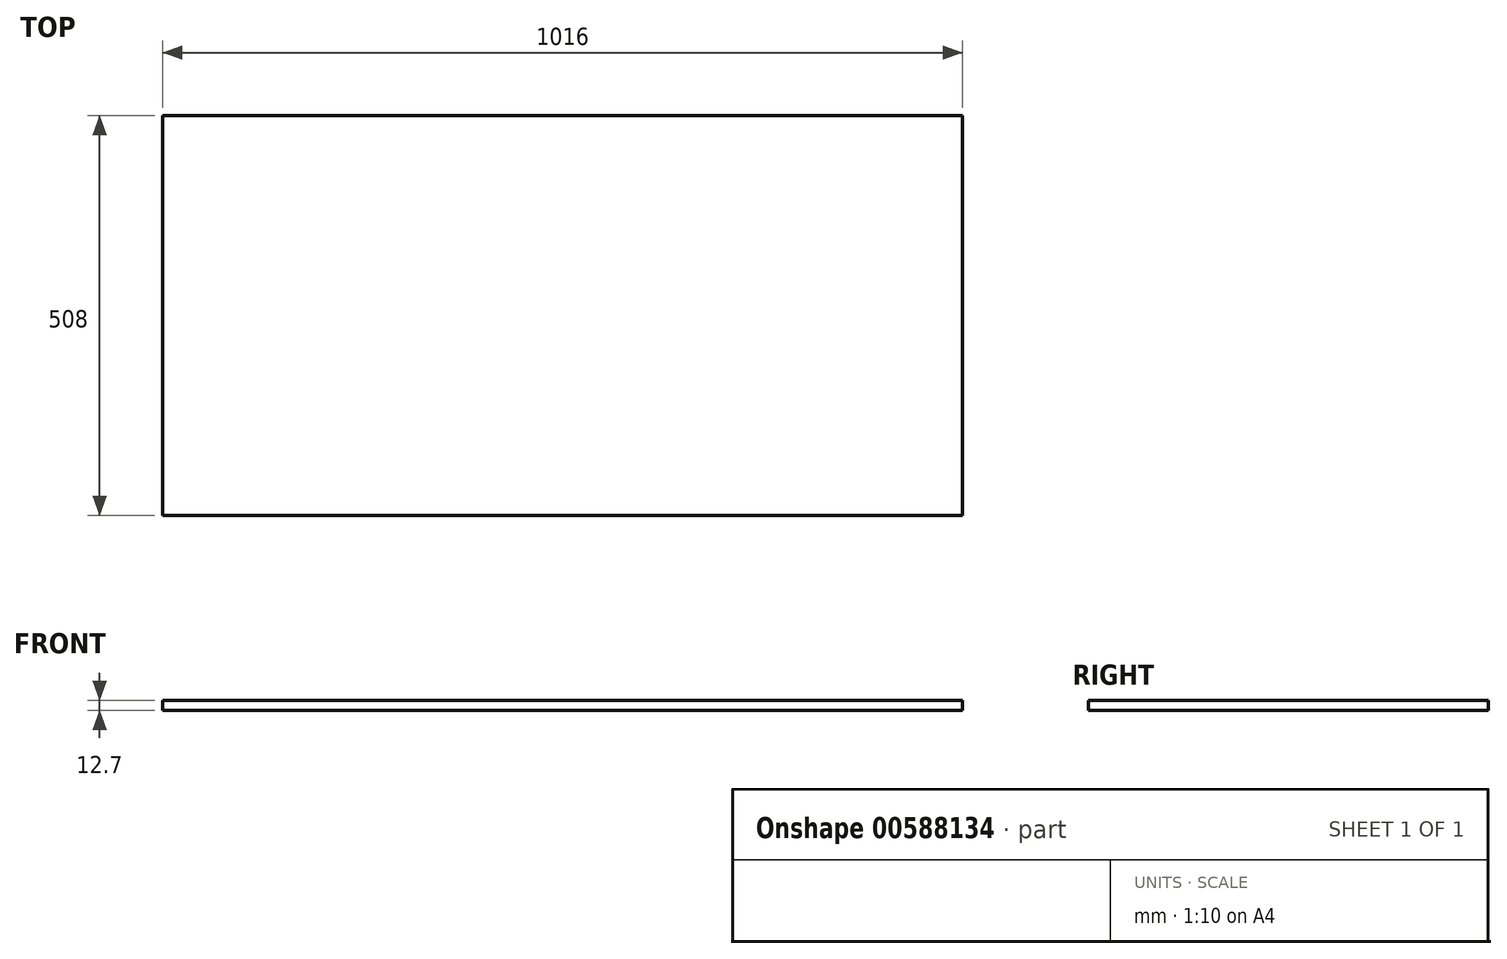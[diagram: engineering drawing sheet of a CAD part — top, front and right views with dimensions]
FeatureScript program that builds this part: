
annotation { "Feature Type Name" : "Feature", "Feature Type Description" : "" }
export const myFeature = defineFeature(function(context is Context, id is Id, definition is map)
    precondition{}
    {
        {
            var Q0;
            Q0=qCreatedBy(makeId("Top.planeOp"),FACE);
            var sketch = newSketch(context, id + "F0", { "sketchPlane" : qUnion([Q0])});
            skLineSegment(sketch, "E0.bottom", {"start": v(-508, 254) * mm, "end": v(508, 254) * mm});
            skLineSegment(sketch, "E0.top", {"start": v(-508, -254) * mm, "end": v(508, -254) * mm});
            skLineSegment(sketch, "E0.left", {"start": v(-508, 254) * mm, "end": v(-508, -254) * mm});
            skLineSegment(sketch, "E0.right", {"start": v(508, 254) * mm, "end": v(508, -254) * mm});
            skPoint(sketch, "E0.middle", {"position": v(0, 0) * mm});
            skSolve(sketch);
        }
        {
            var Q0;
            Q0 = qSketchRegion(id + "F0", true);
            extrude(context, id + "F1", {"entities" : qUnion([Q0]), "endBound" : BoundingType.SYMMETRIC, "depth" : 12.7 * mm, "offsetDistance" : 25.4 * mm});
        }
        {
            var Q0;
            Q0=qCreatedBy(makeId("Right.planeOp"),FACE);
            var sketch = newSketch(context, id + "F2", { "sketchPlane" : qUnion([Q0])});
            skLineSegment(sketch, "E1.bottom", {"start": v(253.5, 0) * mm, "end": v(-254.5, 0) * mm});
            skLineSegment(sketch, "E1.top", {"start": v(253.5, 660.4) * mm, "end": v(-254.5, 660.4) * mm});
            skLineSegment(sketch, "E1.left", {"start": v(253.5, 0) * mm, "end": v(253.5, 660.4) * mm});
            skLineSegment(sketch, "E1.right", {"start": v(-254.5, 0) * mm, "end": v(-254.5, 660.4) * mm});
            skSolve(sketch);
        }
        {
            var Q0;
            Q0=sQuery(id+"F2.wireOp",EDGE,"E1.top");
            var Q1;
            Q1=sQuery(id+"F2.wireOp",EDGE,"E1.right");
            extrude(context, id + "F3", {"bodyType" : ToolBodyType.SURFACE, "surfaceEntities" : qUnion([Q0, Q1]), "endBound" : BoundingType.SYMMETRIC, "depth" : 12.7 * mm, "offsetDistance" : 25.4 * mm});
        }
    });
